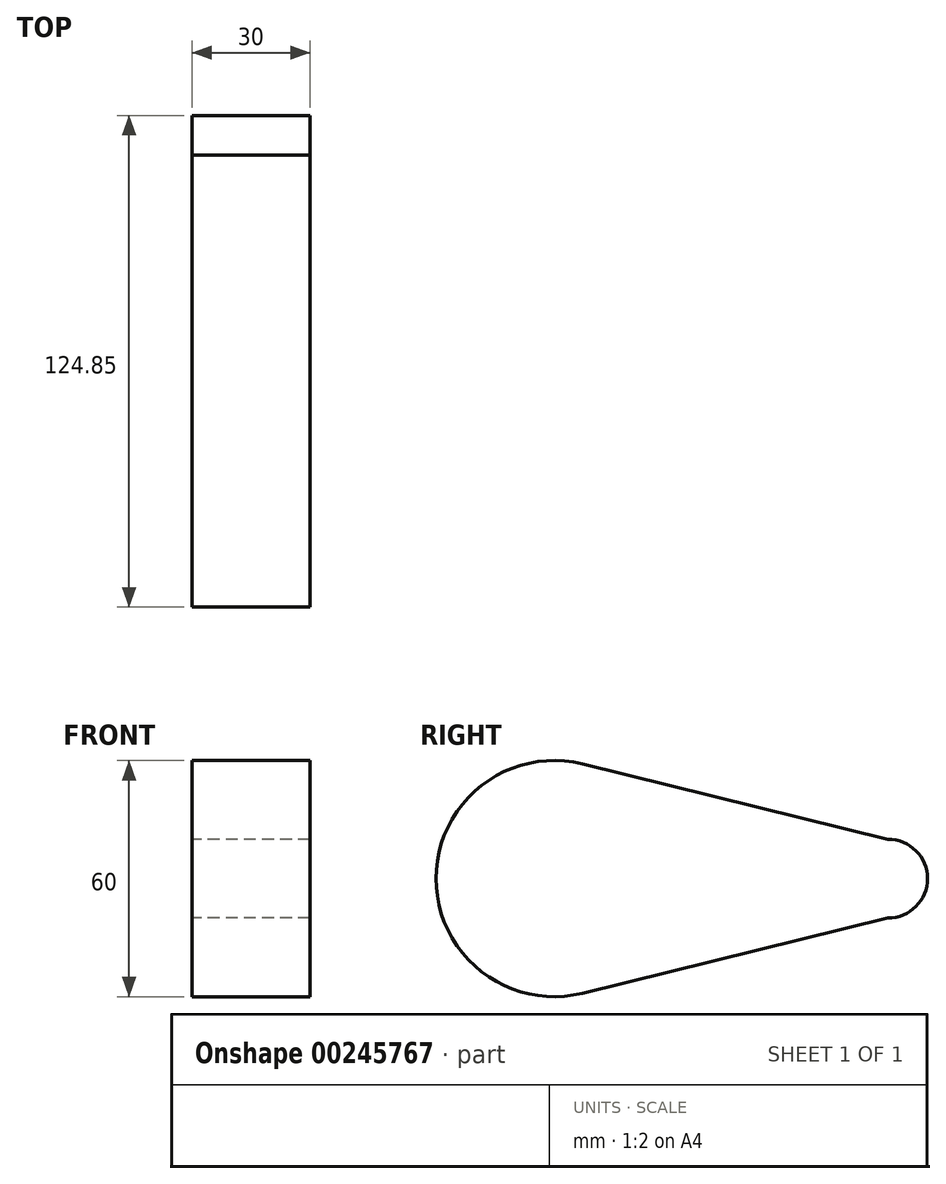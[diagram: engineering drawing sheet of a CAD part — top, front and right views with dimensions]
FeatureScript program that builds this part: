
annotation { "Feature Type Name" : "Feature", "Feature Type Description" : "" }
export const myFeature = defineFeature(function(context is Context, id is Id, definition is map)
    precondition{}
    {
        {
            var Q0;
            Q0=qCreatedBy(makeId("Right.planeOp"),FACE);
            var sketch = newSketch(context, id + "F0", { "sketchPlane" : qUnion([Q0])});
            skCircle(sketch, "E0", {"center": v(-44.22, -26.2) * mm, "radius": 30 * mm});
            skCircle(sketch, "E1", {"center": v(40.63, -26.2) * mm, "radius": 10 * mm});
            skLineSegment(sketch, "E2", {"start": v(40.63, -36.2) * mm, "end": v(-37.05, -55.32) * mm});
            skLineSegment(sketch, "E3", {"start": v(40.63, -16.2) * mm, "end": v(-37.05, 2.94) * mm});
            skText(sketch, "E4", { "text": "Gundam", "fontName": "OpenSans-Bold.ttf"});
            const initialGuessF0  = {"E4": [-0.10358, 0.0389, 1, 0, 0.03676]};
            skSetInitialGuess(sketch, initialGuessF0);
            skSolve(sketch);
        }
        {
            var Q0;
            {var subQ0=sQuery(id+"F0.wireOp",EDGE,"E0");var subQ1=makeQuery(id+"F0.imprint","INTERSECT",VERTEX,{"derivedFrom":[subQ0,sQuery(id+"F0.wireOp",EDGE,"E2")]});Q0=makeQuery(id+"F0.imprint","IMPRINT",FACE,{"disambiguationData":[TD([[makeQuery(id+"F0.imprint","IMPRINT",EDGE,{"disambiguationData":[TD([[subQ1,1.0]])],"derivedFrom":subQ0}),1.0]])]});}
            var Q1;
            {var subQ0=sQuery(id+"F0.wireOp",EDGE,"E2");Q1=makeQuery(id+"F0.imprint","IMPRINT",FACE,{"disambiguationData":[TD([[makeQuery(id+"F0.imprint","IMPRINT",EDGE,{"derivedFrom":subQ0}),-1.0]])]});}
            var Q2;
            {var subQ0=sQuery(id+"F0.wireOp",EDGE,"E1");var subQ1=makeQuery(id+"F0.imprint","INTERSECT",VERTEX,{"derivedFrom":[subQ0,sQuery(id+"F0.wireOp",EDGE,"E2")]});Q2=makeQuery(id+"F0.imprint","IMPRINT",FACE,{"disambiguationData":[TD([[makeQuery(id+"F0.imprint","IMPRINT",EDGE,{"disambiguationData":[TD([[subQ1,1.0]])],"derivedFrom":subQ0}),1.0]])]});}
            extrude(context, id + "F1", {"entities" : qUnion([Q0, Q1, Q2]), "depth" : 30 * mm});
        }
    });
